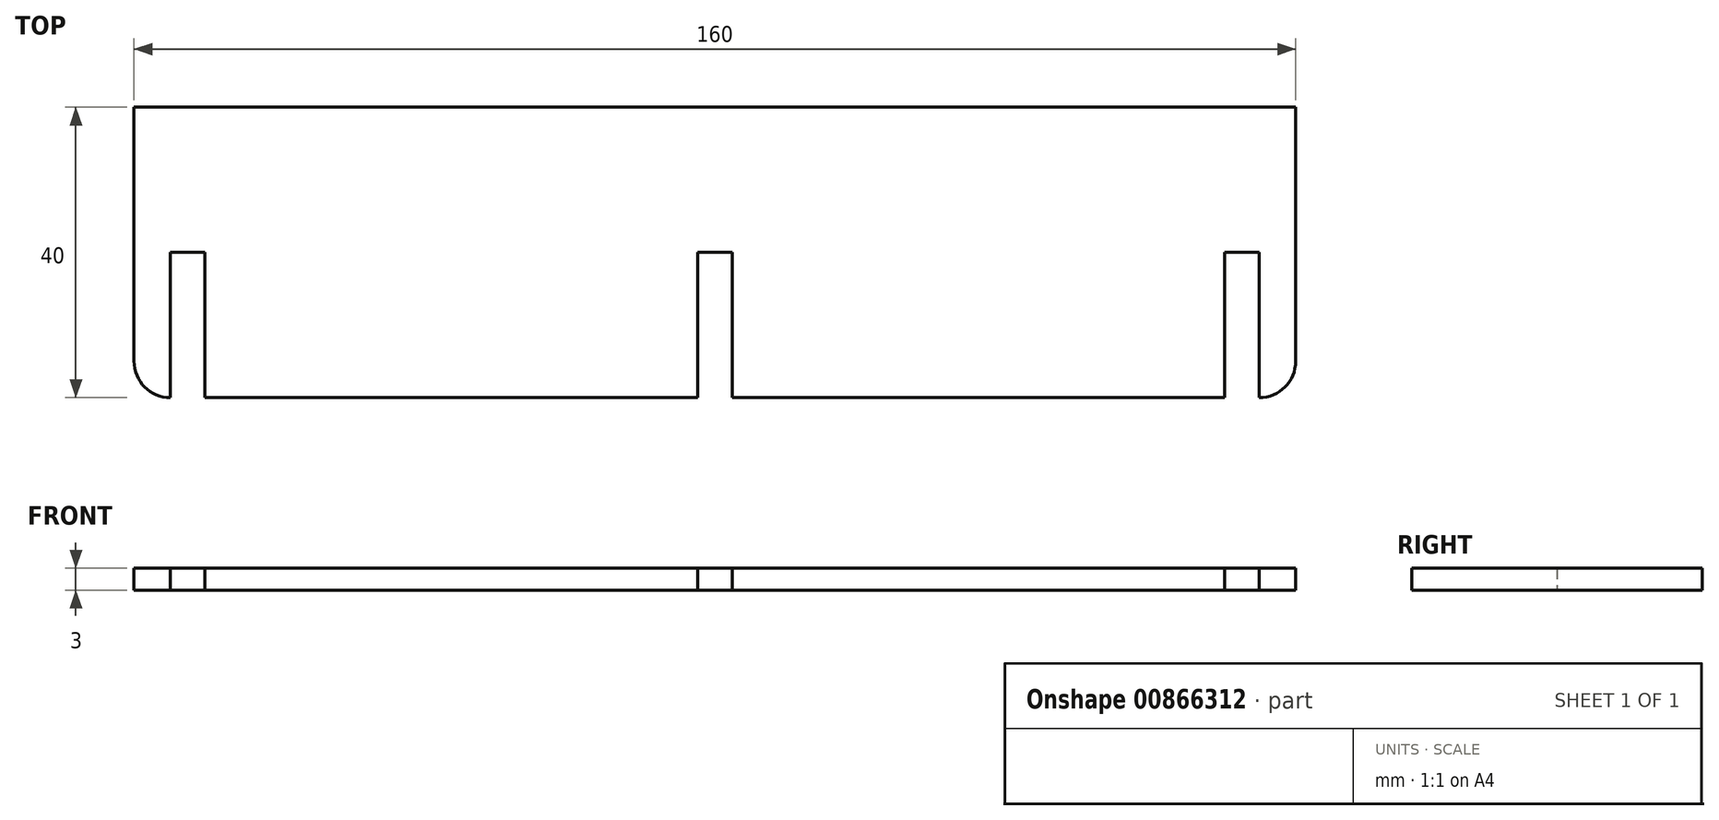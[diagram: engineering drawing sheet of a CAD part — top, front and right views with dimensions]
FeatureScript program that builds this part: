
annotation { "Feature Type Name" : "Feature", "Feature Type Description" : "" }
export const myFeature = defineFeature(function(context is Context, id is Id, definition is map)
    precondition{}
    {
        {
            var Q0;
            Q0=qCreatedBy(makeId("Top.planeOp"),FACE);
            var sketch = newSketch(context, id + "F0", { "sketchPlane" : qUnion([Q0])});
            skLineSegment(sketch, "E0.bottom", {"start": v(-80, 20) * mm, "end": v(80, 20) * mm});
            skLineSegment(sketch, "E0.top", {"start": v(-75, -20) * mm, "end": v(75, -20) * mm});
            skLineSegment(sketch, "E0.left", {"start": v(-80, 20) * mm, "end": v(-80, -15) * mm});
            skLineSegment(sketch, "E0.right", {"start": v(80, 20) * mm, "end": v(80, -15) * mm});
            skPoint(sketch, "E0.middle", {"position": v(0, 0) * mm});
            skPoint(sketch, "E1", {"position": v(-75, -20) * mm});
            skPoint(sketch, "E2", {"position": v(0, -20) * mm});
            skPoint(sketch, "E3", {"position": v(75, -20) * mm});
            skLineSegment(sketch, "E4", {"start": v(-75, -20) * mm, "end": v(-75, 0) * mm});
            skLineSegment(sketch, "E5", {"start": v(-75, 0) * mm, "end": v(-70.25, 0) * mm});
            skLineSegment(sketch, "E6", {"start": v(-70.25, 0) * mm, "end": v(-70.25, -20) * mm});
            skLineSegment(sketch, "E7", {"start": v(-75, -20) * mm, "end": v(-70.25, -20) * mm});
            skLineSegment(sketch, "E8.1.0.0", {"start": v(2.38, 0) * mm, "end": v(2.38, -20) * mm});
            skLineSegment(sketch, "E8.1.0.1", {"start": v(-2.37, 0) * mm, "end": v(2.38, 0) * mm});
            skLineSegment(sketch, "E8.1.0.2", {"start": v(-2.37, -20) * mm, "end": v(-2.37, 0) * mm});
            skLineSegment(sketch, "E8.2.0.0", {"start": v(75, 0) * mm, "end": v(75, -20) * mm});
            skLineSegment(sketch, "E8.2.0.1", {"start": v(70.25, 0) * mm, "end": v(75, 0) * mm});
            skLineSegment(sketch, "E8.2.0.2", {"start": v(70.25, -20) * mm, "end": v(70.25, 0) * mm});
            skLineSegment(sketch, "E8.direction1", {"start": v(-75, -20) * mm, "end": v(-2.37, -20) * mm, "construction": true});
            skPoint(sketch, "E9.visualSharp", {"position": v(-80, -20) * mm});
            skArc(sketch, "E9.filletArc", {"start": v(-80, -15) * mm, "mid": v(-78.54, -18.54) * mm, "end": v(-75, -20) * mm});
            skPoint(sketch, "E10.visualSharp", {"position": v(80, -20) * mm});
            skArc(sketch, "E10.filletArc", {"start": v(75, -20) * mm, "mid": v(78.54, -18.54) * mm, "end": v(80, -15) * mm});
            skSolve(sketch);
        }
        {
            var Q0;
            Q0=makeQuery(id+"F0.imprint","IMPRINT",FACE,{"disambiguationData":[TD([[makeQuery(id+"F0.imprint","IMPRINT",EDGE,{"derivedFrom":sQuery(id+"F0.wireOp",EDGE,"E0.bottom")}),-1.0]])]});
            extrude(context, id + "F1", {"entities" : qUnion([Q0]), "depth" : 3 * mm, "offsetDistance" : 25 * mm});
        }
    });
